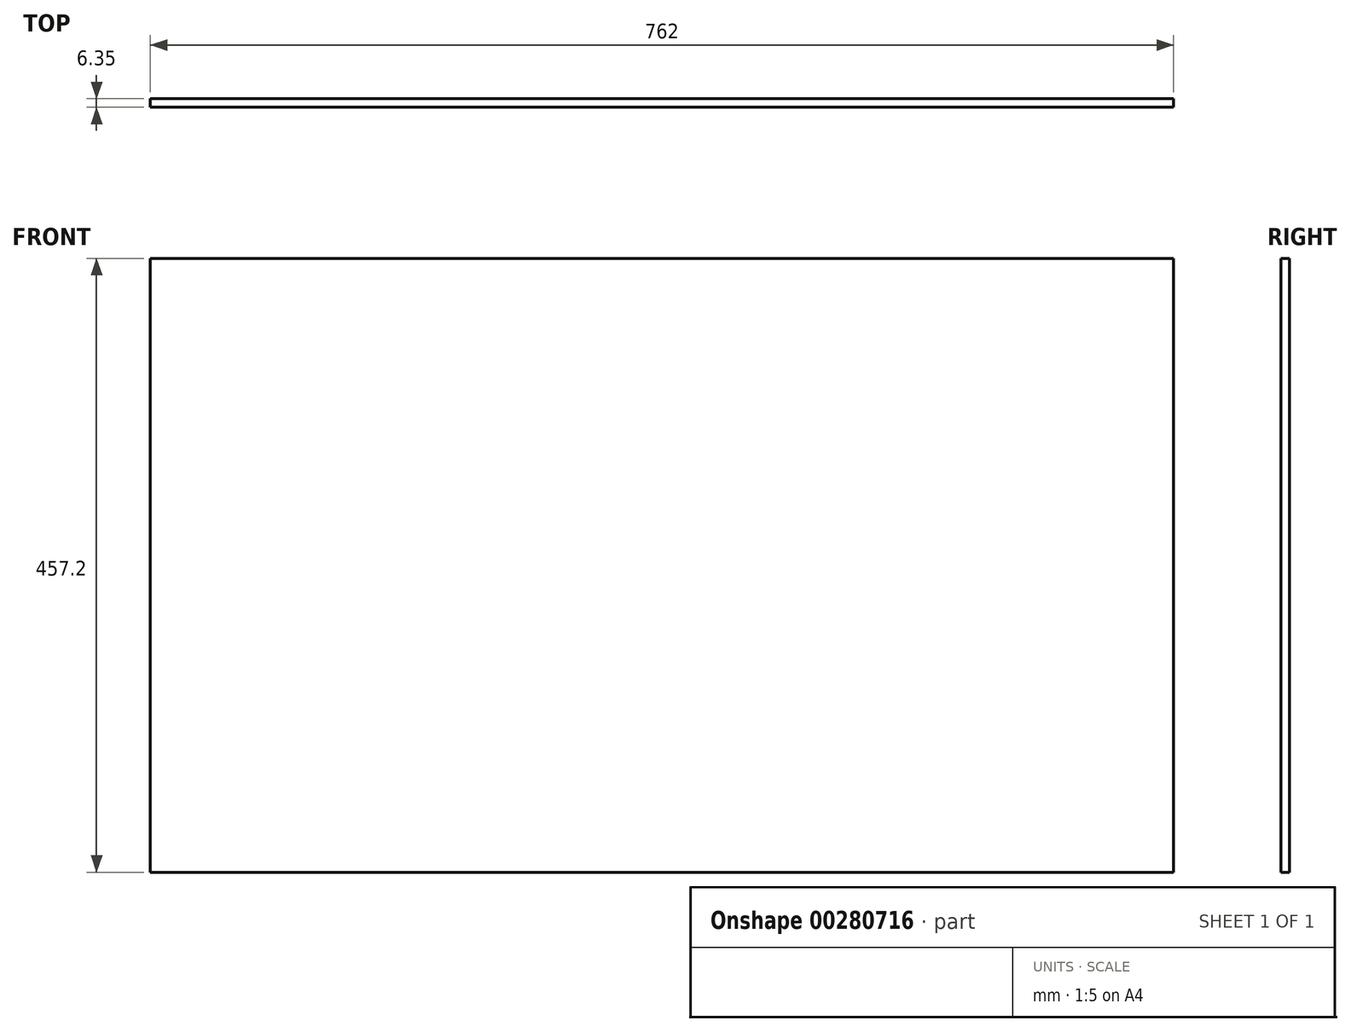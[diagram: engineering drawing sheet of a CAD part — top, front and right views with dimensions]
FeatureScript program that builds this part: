
annotation { "Feature Type Name" : "Feature", "Feature Type Description" : "" }
export const myFeature = defineFeature(function(context is Context, id is Id, definition is map)
    precondition{}
    {
        {
            var Q0;
            Q0=qCreatedBy(makeId("Front.planeOp"),FACE);
            var sketch = newSketch(context, id + "F0", { "sketchPlane" : qUnion([Q0])});
            skLineSegment(sketch, "E0.bottom", {"start": v(-381, 228.6) * mm, "end": v(381, 228.6) * mm});
            skLineSegment(sketch, "E0.top", {"start": v(-381, -228.6) * mm, "end": v(381, -228.6) * mm});
            skLineSegment(sketch, "E0.left", {"start": v(-381, 228.6) * mm, "end": v(-381, -228.6) * mm});
            skLineSegment(sketch, "E0.right", {"start": v(381, 228.6) * mm, "end": v(381, -228.6) * mm});
            skPoint(sketch, "E0.middle", {"position": v(0, 0) * mm});
            skSolve(sketch);
        }
        {
            var Q0;
            Q0=makeQuery(id+"F0.imprint","IMPRINT",FACE,{"disambiguationData":[TD([[makeQuery(id+"F0.imprint","IMPRINT",EDGE,{"derivedFrom":sQuery(id+"F0.wireOp",EDGE,"E0.bottom")}),-1.0]])]});
            extrude(context, id + "F1", {"entities" : qUnion([Q0]), "depth" : 6.35 * mm});
        }
    });
